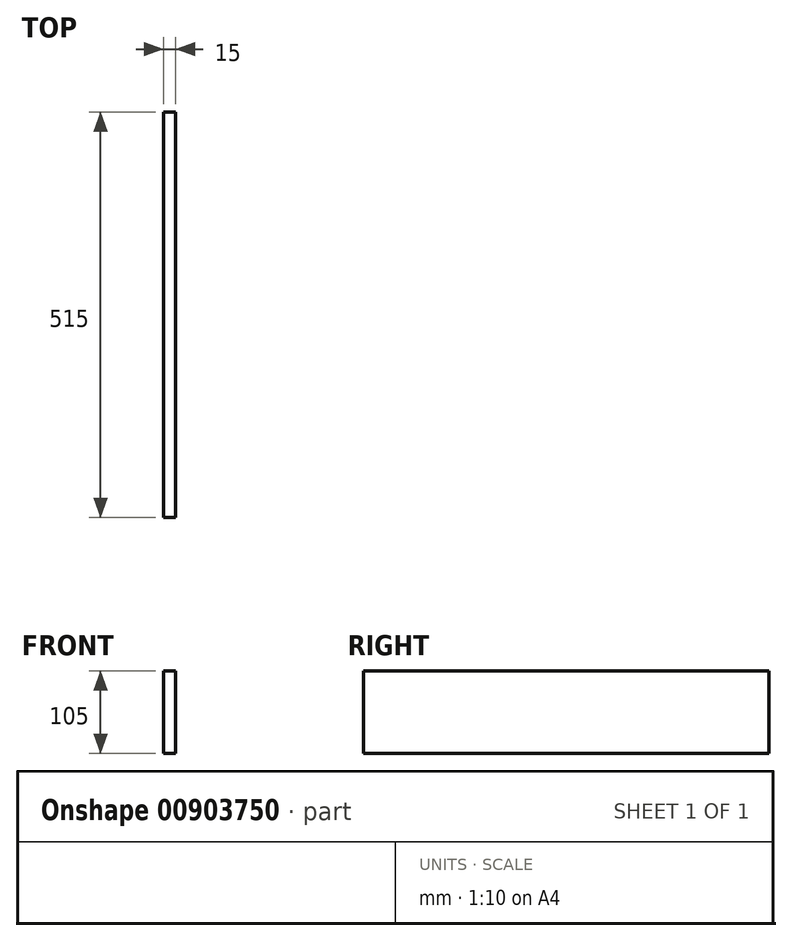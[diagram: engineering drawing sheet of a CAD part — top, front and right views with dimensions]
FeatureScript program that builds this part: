
annotation { "Feature Type Name" : "Feature", "Feature Type Description" : "" }
export const myFeature = defineFeature(function(context is Context, id is Id, definition is map)
    precondition{}
    {
        {
            var Q0;
            Q0=qCreatedBy(makeId("Right.planeOp"),FACE);
            var sketch = newSketch(context, id + "F0", { "sketchPlane" : qUnion([Q0])});
            skLineSegment(sketch, "E0.bottom", {"start": v(-257.5, 52.5) * mm, "end": v(257.5, 52.5) * mm});
            skLineSegment(sketch, "E0.top", {"start": v(-257.5, -52.5) * mm, "end": v(257.5, -52.5) * mm});
            skLineSegment(sketch, "E0.left", {"start": v(-257.5, 52.5) * mm, "end": v(-257.5, -52.5) * mm});
            skLineSegment(sketch, "E0.right", {"start": v(257.5, 52.5) * mm, "end": v(257.5, -52.5) * mm});
            skSolve(sketch);
        }
        {
            var Q0;
            Q0=makeQuery(id+"F0.imprint","IMPRINT",FACE,{"disambiguationData":[TD([[makeQuery(id+"F0.imprint","IMPRINT",EDGE,{"derivedFrom":sQuery(id+"F0.wireOp",EDGE,"E0.bottom")}),-1.0]])]});
            extrude(context, id + "F1", {"entities" : qUnion([Q0]), "depth" : 15 * mm, "offsetDistance" : 25 * mm});
        }
    });
